# Revit family: BIMLIB_ОбратныйКлапан_RSK_SHUFT
name_source: partatom
category: Арматура воздуховодов
revit_build: Autodesk Revit 2017 (Build: 20170118_1100(x64)
units: mm (PartAtom-declared; Revit-internal decimal feet)

## family parameters
Всегда вертикально = Да
На основе рабочей плоскости = Нет
Общий = Нет
При загрузке вырезать с полостями = Нет
Размер круглого соединителя = Использовать диаметр
Тип детали = Вставляется

## types (1)
- BIMLIB_ОбратныйКлапан_RSK_SHUFT
    ADSK_URL документации изделия = http://www.shuft.ru
    ADSK_URL страницы изделия = http://www.shuft.ru
    ADSK_Версия Revit = 2017
    ADSK_Версия семейства = v.1
    ADSK_Единица измерения = шт.
    ADSK_Завод-изготовитель = ООО «Завод ВКО» марка SHUFT
    ADSK_Материал = BIMLIB_Сталь_SHUFT
    BL_BIM library = https://bimlib.pro
    URL = http://www.shuft.ru
    Изготовитель = ООО «Завод ВКО» марка SHUFT
    Описание = Обратные клапаны с подпружиненными лопастями серии RSK предназначены для автоматического перерывания круглых воздуховодов при отключении систем вентиляции. Корпус клапана выполнен из оцинкованной стали, лопасти — из листового алюминия. Крепление клапана к другим элементам системы вентиляции производится при помощи ниппельного соединения. Клапан может быть установлен в вертикальном положении.
    Таблица = RSK
